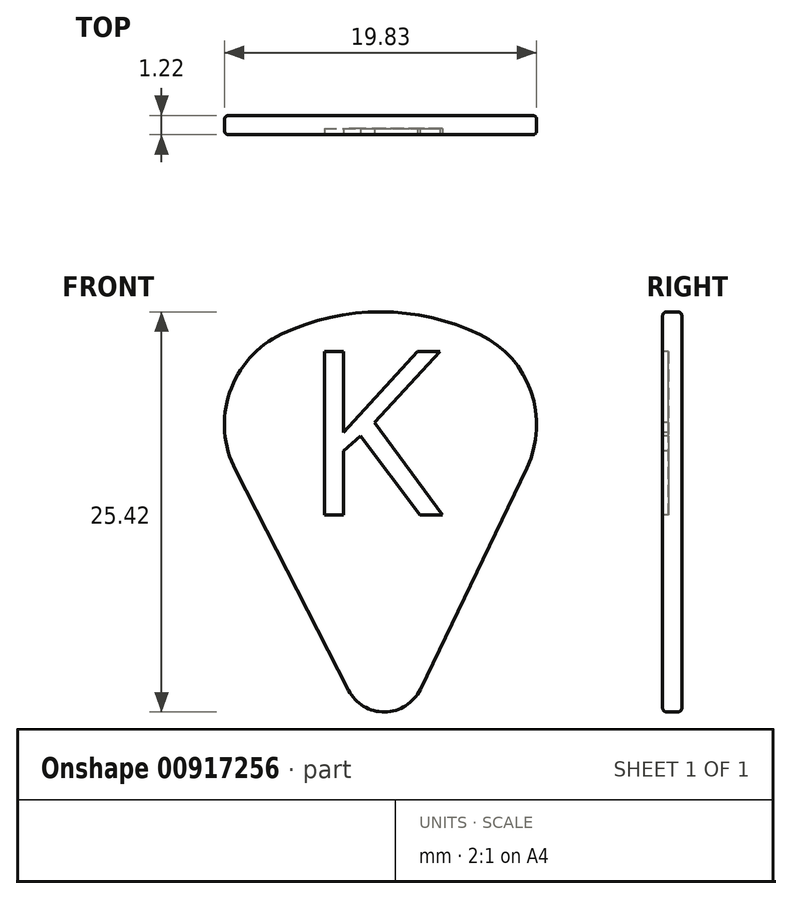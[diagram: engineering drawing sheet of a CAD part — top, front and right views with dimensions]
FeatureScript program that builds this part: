
annotation { "Feature Type Name" : "Feature", "Feature Type Description" : "" }
export const myFeature = defineFeature(function(context is Context, id is Id, definition is map)
    precondition{}
    {
        {
            var Q0;
            Q0=qCreatedBy(makeId("Front.planeOp"),FACE);
            var sketch = newSketch(context, id + "F0", { "sketchPlane" : qUnion([Q0])});
            skLineSegment(sketch, "E0", {"start": v(-22.58, 35.4) * mm, "end": v(-15.4, 21.41) * mm});
            skLineSegment(sketch, "E1", {"start": v(-10.85, 21.47) * mm, "end": v(-4.09, 35.52) * mm});
            skArc(sketch, "E2", {"start": v(-7.05, 44) * mm, "mid": v(-13.36, 45.45) * mm, "end": v(-19.67, 44.03) * mm});
            skPoint(sketch, "E3.visualSharp", {"position": v(-24.88, 39.85) * mm});
            skArc(sketch, "E3.filletArc", {"start": v(-19.67, 44.03) * mm, "mid": v(-22.95, 40.32) * mm, "end": v(-22.58, 35.4) * mm});
            skPoint(sketch, "E4.visualSharp", {"position": v(-1.96, 39.93) * mm});
            skArc(sketch, "E4.filletArc", {"start": v(-4.09, 35.52) * mm, "mid": v(-3.81, 40.37) * mm, "end": v(-7.05, 44) * mm});
            skPoint(sketch, "E5.visualSharp", {"position": v(-13.06, 16.87) * mm});
            skArc(sketch, "E5.filletArc", {"start": v(-15.4, 21.41) * mm, "mid": v(-13.1, 20.03) * mm, "end": v(-10.85, 21.47) * mm});
            skSolve(sketch);
        }
        {
            var Q0;
            Q0=makeQuery(id+"F0.imprint","IMPRINT",FACE,{"disambiguationData":[TD([[makeQuery(id+"F0.imprint","IMPRINT",EDGE,{"derivedFrom":sQuery(id+"F0.wireOp",EDGE,"E0")}),1.0]])]});
            extrude(context, id + "F1", {"entities" : qUnion([Q0]), "depth" : 1.22 * mm, "offsetDistance" : 25.4 * mm});
        }
        {
            var Q0;
            Q0=makeQuery(id+"F1.opExtrude","CAP_EDGE",EDGE,{"disambiguationData":[OSD([sQuery(id+"F0.wireOp",EDGE,"E1")])],"isStart":true});
            var Q1;
            Q1=makeQuery(id+"F1.opExtrude","CAP_EDGE",EDGE,{"disambiguationData":[OSD([sQuery(id+"F0.wireOp",EDGE,"E0")])],"isStart":false});
            var Q2;
            {var subQ0=sQuery(id+"F0.wireOp",EDGE,"E1");var subQ1=sQuery(id+"F0.wireOp",EDGE,"E0");Q2=makeQuery(id+"FKY3l0F4HxnJszU_1.opFillet","BLEND_EDGE",EDGE,{"blendedFrom":[makeQuery(id+"F1.opExtrude","SWEPT_EDGE",EDGE,{"disambiguationData":[OSD([subQ1,subQ0])]}),makeQuery(id+"F1.opExtrude","CAP_FACE",FACE,{"disambiguationData":[OSD([subQ1,subQ0,sQuery(id+"F0.wireOp",EDGE,"E2"),sQuery(id+"F0.wireOp",EDGE,"E3.filletArc"),sQuery(id+"F0.wireOp",EDGE,"E4.filletArc")])],"isStart":true})],"blendedInto":[makeQuery(id+"F1.opExtrude","CAP_FACE",FACE,{"disambiguationData":[OSD([subQ1,subQ0,sQuery(id+"F0.wireOp",EDGE,"E2"),sQuery(id+"F0.wireOp",EDGE,"E3.filletArc"),sQuery(id+"F0.wireOp",EDGE,"E4.filletArc")])],"isStart":true})]});}
            var Q3;
            Q3=makeQuery(id+"F1.opExtrude","CAP_EDGE",EDGE,{"disambiguationData":[OSD([sQuery(id+"F0.wireOp",EDGE,"E1")])],"isStart":false});
            var Q4;
            Q4=makeQuery(id+"F1.opExtrude","CAP_EDGE",EDGE,{"disambiguationData":[OSD([sQuery(id+"F0.wireOp",EDGE,"E2")])],"isStart":false});
            var Q5;
            Q5=makeQuery(id+"F1.opExtrude","CAP_FACE",FACE,{"disambiguationData":[OSD([sQuery(id+"F0.wireOp",EDGE,"E0"),sQuery(id+"F0.wireOp",EDGE,"E1"),sQuery(id+"F0.wireOp",EDGE,"E2"),sQuery(id+"F0.wireOp",EDGE,"E3.filletArc"),sQuery(id+"F0.wireOp",EDGE,"E4.filletArc")])],"isStart":false});
            var Q6;
            Q6=makeQuery(id+"F1.opExtrude","CAP_EDGE",EDGE,{"disambiguationData":[OSD([sQuery(id+"F0.wireOp",EDGE,"E4.filletArc")])],"isStart":true});
            var Q7;
            Q7=makeQuery(id+"F1.opExtrude","CAP_EDGE",EDGE,{"disambiguationData":[OSD([sQuery(id+"F0.wireOp",EDGE,"E2")])],"isStart":true});
            var Q8;
            Q8=makeQuery(id+"F1.opExtrude","CAP_EDGE",EDGE,{"disambiguationData":[OSD([sQuery(id+"F0.wireOp",EDGE,"E3.filletArc")])],"isStart":true});
            var Q9;
            Q9=makeQuery(id+"F1.opExtrude","CAP_EDGE",EDGE,{"disambiguationData":[OSD([sQuery(id+"F0.wireOp",EDGE,"E0")])],"isStart":true});
            fillet(context, id + "F2", {"entities" : qUnion([Q0, Q1, Q2, Q3, Q4, Q5, Q6, Q7, Q8, Q9]), "radius" : 0.25 * mm, "tangentPropagation" : true, "allowEdgeOverflow" : false});
        }
        {
            var Q0;
            Q0=makeQuery(id+"F1.opExtrude","CAP_FACE",FACE,{"disambiguationData":[OSD([sQuery(id+"F0.wireOp",EDGE,"E0"),sQuery(id+"F0.wireOp",EDGE,"E1"),sQuery(id+"F0.wireOp",EDGE,"E2"),sQuery(id+"F0.wireOp",EDGE,"E3.filletArc"),sQuery(id+"F0.wireOp",EDGE,"E4.filletArc")])],"isStart":false});
            var sketch = newSketch(context, id + "F3", { "sketchPlane" : qUnion([Q0])});
            skText(sketch, "E6", { "text": "K", "fontName": "OpenSans-Regular.ttf"});
            skPoint(sketch, "E7.startSnap0", {"position": v(-13.36, 45.2) * mm});
            const initialGuessF3  = {"E6": [-0.01836, 0.03254, 1, 0, 0.01047]};
            skSetInitialGuess(sketch, initialGuessF3);
            skSolve(sketch);
        }
        {
            var Q0;
            Q0 = qSketchRegion(id + "F3", true);
            extrude(context, id + "F4", {"entities" : qUnion([Q0]), "operationType" : NewBodyOperationType.REMOVE, "oppositeDirection" : true, "depth" : 0.38 * mm, "offsetDistance" : 25.4 * mm});
        }
    });
